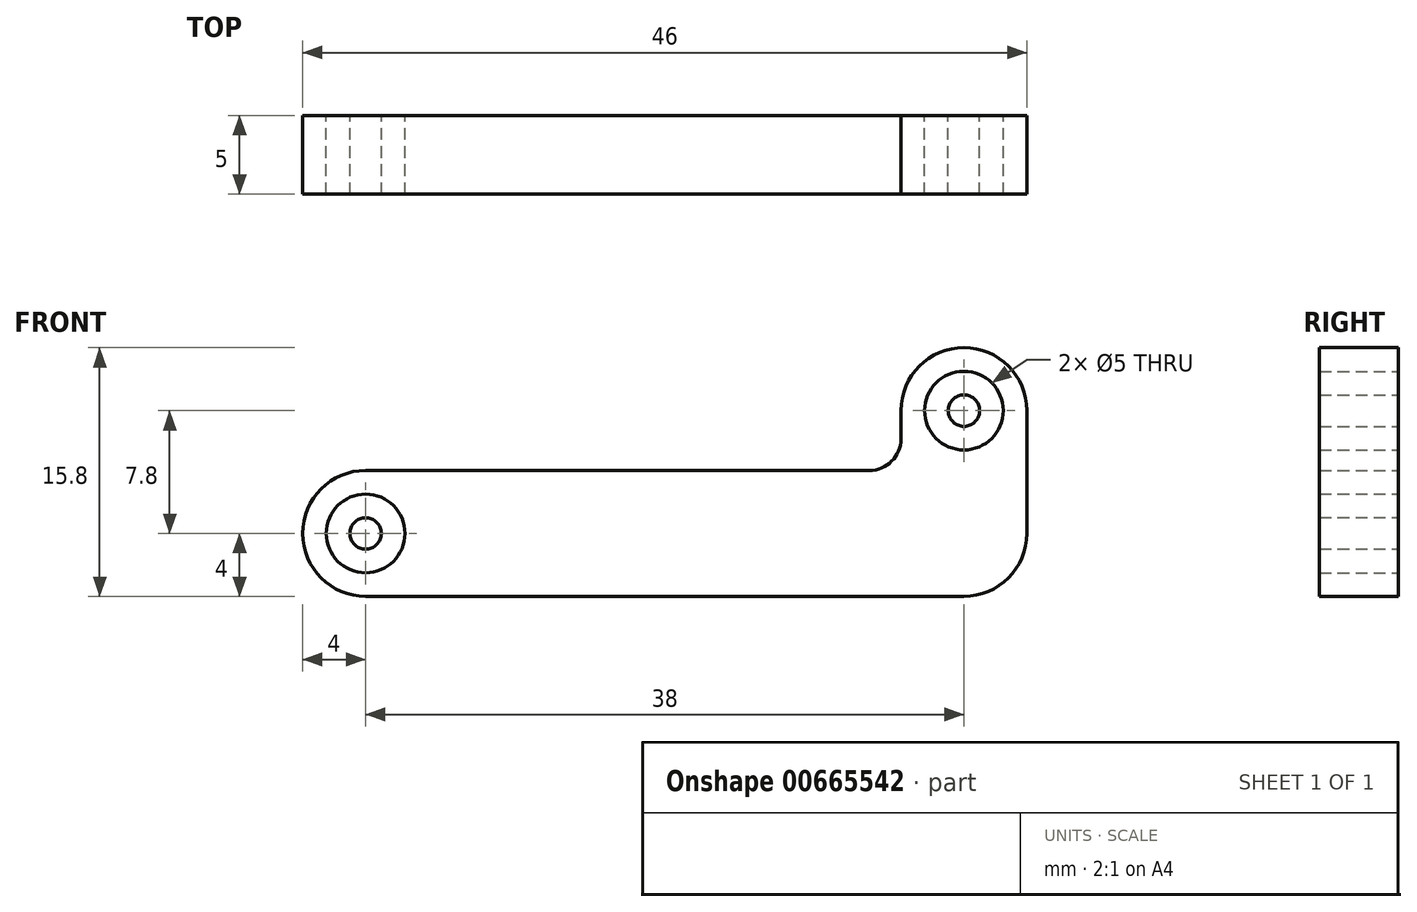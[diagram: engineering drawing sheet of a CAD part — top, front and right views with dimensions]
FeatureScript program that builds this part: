
annotation { "Feature Type Name" : "Feature", "Feature Type Description" : "" }
export const myFeature = defineFeature(function(context is Context, id is Id, definition is map)
    precondition{}
    {
        {
            var Q0;
            Q0=qCreatedBy(makeId("Front.planeOp"),FACE);
            var sketch = newSketch(context, id + "F0", { "sketchPlane" : qUnion([Q0])});
            skArc(sketch, "E0", {"start": v(0, 4) * mm, "mid": v(-4, 0) * mm, "end": v(0, -4) * mm});
            skCircle(sketch, "E1", {"center": v(0, 0) * mm, "radius": 2.5 * mm});
            skCircle(sketch, "E2", {"center": v(0, 0) * mm, "radius": 1 * mm});
            skArc(sketch, "E3", {"start": v(42, 7.8) * mm, "mid": v(38, 11.8) * mm, "end": v(34, 7.8) * mm});
            skCircle(sketch, "E4", {"center": v(38, 7.8) * mm, "radius": 2.5 * mm});
            skCircle(sketch, "E5", {"center": v(38, 7.8) * mm, "radius": 1 * mm});
            skLineSegment(sketch, "E6", {"start": v(0, 4) * mm, "end": v(32, 4) * mm});
            skLineSegment(sketch, "E7", {"start": v(34, 7.8) * mm, "end": v(34, 6) * mm});
            skLineSegment(sketch, "E8.0", {"start": v(0, -4) * mm, "end": v(38, -4) * mm});
            skLineSegment(sketch, "E9", {"start": v(42, 7.8) * mm, "end": v(42, 0) * mm});
            skPoint(sketch, "E10.visualSharp", {"position": v(34, 4) * mm});
            skArc(sketch, "E10.filletArc", {"start": v(32, 4) * mm, "mid": v(33.41, 4.59) * mm, "end": v(34, 6) * mm});
            skPoint(sketch, "E11.visualSharp", {"position": v(42, -4) * mm});
            skArc(sketch, "E11.filletArc", {"start": v(38, -4) * mm, "mid": v(40.83, -2.83) * mm, "end": v(42, 0) * mm});
            skSolve(sketch);
        }
        {
            var Q0;
            Q0 = qSketchRegion(id + "F0", true);
            var Q1;
            Q1=makeQuery(id+"F0.imprint","IMPRINT",FACE,{"disambiguationData":[TD([[makeQuery(id+"F0.imprint","IMPRINT",EDGE,{"derivedFrom":sQuery(id+"F0.wireOp",EDGE,"E5")}),1.0]])]});
            var Q2;
            Q2=makeQuery(id+"F0.imprint","IMPRINT",FACE,{"disambiguationData":[TD([[makeQuery(id+"F0.imprint","IMPRINT",EDGE,{"derivedFrom":sQuery(id+"F0.wireOp",EDGE,"E2")}),1.0]])]});
            extrude(context, id + "F1", {"entities" : qUnion([Q0, Q1, Q2]), "depth" : 5 * mm, "offsetDistance" : 25 * mm});
        }
    });
